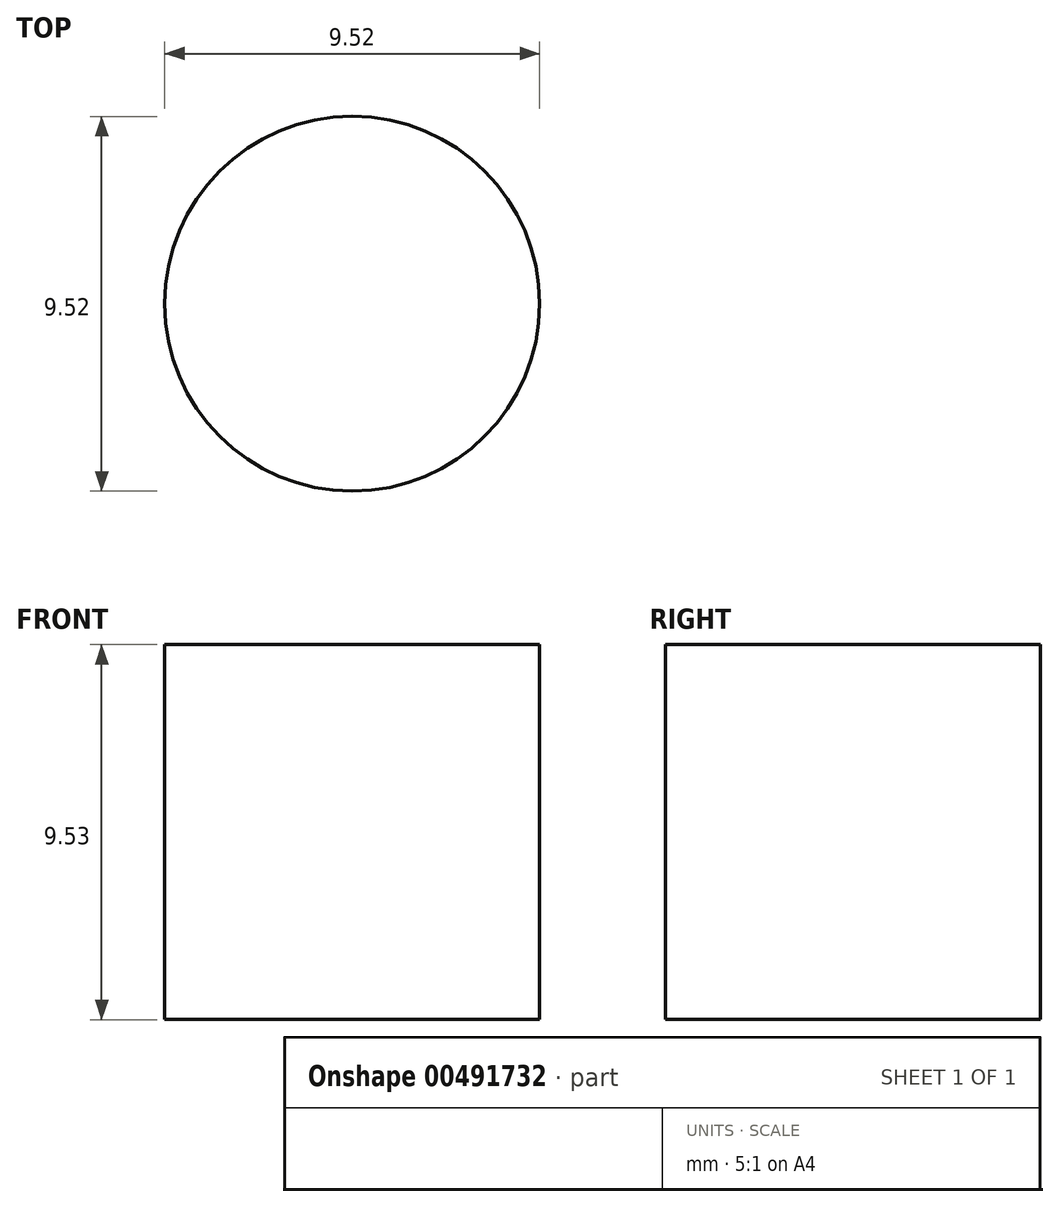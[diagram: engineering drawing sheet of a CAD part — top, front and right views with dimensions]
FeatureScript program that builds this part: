
annotation { "Feature Type Name" : "Feature", "Feature Type Description" : "" }
export const myFeature = defineFeature(function(context is Context, id is Id, definition is map)
    precondition{}
    {
        {
            var Q0;
            Q0=qCreatedBy(makeId("Front.planeOp"),FACE);
            var sketch = newSketch(context, id + "F0", { "sketchPlane" : qUnion([Q0])});
            skLineSegment(sketch, "E0", {"start": v(0, 0) * mm, "end": v(0, 57.15) * mm});
            skLineSegment(sketch, "E1", {"start": v(0, 57.15) * mm, "end": v(7.62, 57.15) * mm});
            skLineSegment(sketch, "E2", {"start": v(29.22, 38.1) * mm, "end": v(7.62, 38.1) * mm});
            skLineSegment(sketch, "E3", {"start": v(7.62, 38.1) * mm, "end": v(7.62, 57.15) * mm});
            skLineSegment(sketch, "E4", {"start": v(0, 57.15) * mm, "end": v(4.76, 57.15) * mm});
            skLineSegment(sketch, "E5", {"start": v(4.76, 57.15) * mm, "end": v(4.76, 47.63) * mm});
            skLineSegment(sketch, "E6", {"start": v(4.76, 47.63) * mm, "end": v(0, 47.63) * mm});
            skLineSegment(sketch, "E7", {"start": v(0, 0) * mm, "end": v(0, 21.59) * mm});
            skLineSegment(sketch, "E8", {"start": v(0, 21.59) * mm, "end": v(1.6, 21.59) * mm});
            skLineSegment(sketch, "E9", {"start": v(1.6, 21.59) * mm, "end": v(1.6, 0.6) * mm});
            skLineSegment(sketch, "E10", {"start": v(1.6, 0.6) * mm, "end": v(27.7, 10.48) * mm});
            skLineSegment(sketch, "E11", {"start": v(31.76, 35.57) * mm, "end": v(31.8, 16.44) * mm});
            skPoint(sketch, "E12.visualSharp", {"position": v(31.82, 12.04) * mm});
            skArc(sketch, "E12.filletArc", {"start": v(27.7, 10.48) * mm, "mid": v(30.68, 12.82) * mm, "end": v(31.8, 16.44) * mm});
            skPoint(sketch, "E13.visualSharp", {"position": v(31.75, 38.1) * mm});
            skArc(sketch, "E13.filletArc", {"start": v(31.76, 35.57) * mm, "mid": v(31.01, 37.36) * mm, "end": v(29.22, 38.1) * mm});
            skSolve(sketch);
        }
        {
            var Q0;
            {var subQ0=sQuery(id+"F0.wireOp",EDGE,"OcougQHS-bHDD-pBbX-PTpK-duneQBcOzH4T");Q0=makeQuery(id+"F0.imprint","IMPRINT",FACE,{"disambiguationData":[TD([[makeQuery(id+"F0.imprint","IMPRINT",EDGE,{"derivedFrom":subQ0}),1.0]])]});}
            var Q1;
            Q1=makeQuery(id+"F0.imprint","IMPRINT",FACE,{"disambiguationData":[TD([[makeQuery(id+"F0.imprint","IMPRINT",EDGE,{"derivedFrom":sQuery(id+"F0.wireOp",EDGE,"E1")}),-1.0]])]});
            var Q2;
            Q2=sQuery(id+"F0.wireOp",EDGE,"E0");
            revolve(context, id + "F1", {"entities" : qUnion([Q0, Q1]), "axis" : qUnion([Q2]), "revolveType" : RevolveType.FULL});
        }
    });
